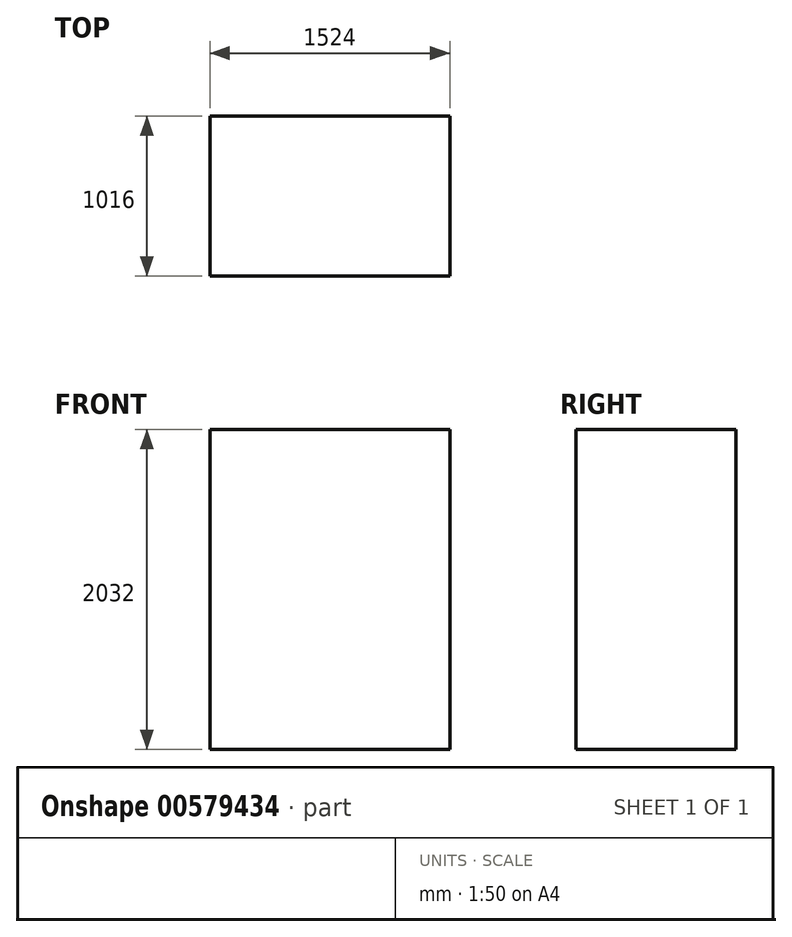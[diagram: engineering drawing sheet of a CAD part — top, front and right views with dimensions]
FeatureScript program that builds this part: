
annotation { "Feature Type Name" : "Feature", "Feature Type Description" : "" }
export const myFeature = defineFeature(function(context is Context, id is Id, definition is map)
    precondition{}
    {
        {
            var Q0;
            Q0=qCreatedBy(makeId("Top.planeOp"),FACE);
            var sketch = newSketch(context, id + "F0", { "sketchPlane" : qUnion([Q0])});
            skLineSegment(sketch, "E0.bottom", {"start": v(0, 0) * mm, "end": v(-1524, 0) * mm});
            skLineSegment(sketch, "E0.top", {"start": v(0, 1016) * mm, "end": v(-1524, 1016) * mm});
            skLineSegment(sketch, "E0.left", {"start": v(0, 0) * mm, "end": v(0, 1016) * mm});
            skLineSegment(sketch, "E0.right", {"start": v(-1524, 0) * mm, "end": v(-1524, 1016) * mm});
            skSolve(sketch);
        }
        {
            var Q0;
            Q0=makeQuery(id+"F0.imprint","IMPRINT",FACE,{"disambiguationData":[TD([[makeQuery(id+"F0.imprint","IMPRINT",EDGE,{"derivedFrom":sQuery(id+"F0.wireOp",EDGE,"E0.bottom")}),-1.0]])]});
            extrude(context, id + "F1", {"entities" : qUnion([Q0]), "depth" : 2032 * mm, "offsetDistance" : 25.4 * mm});
        }
    });
